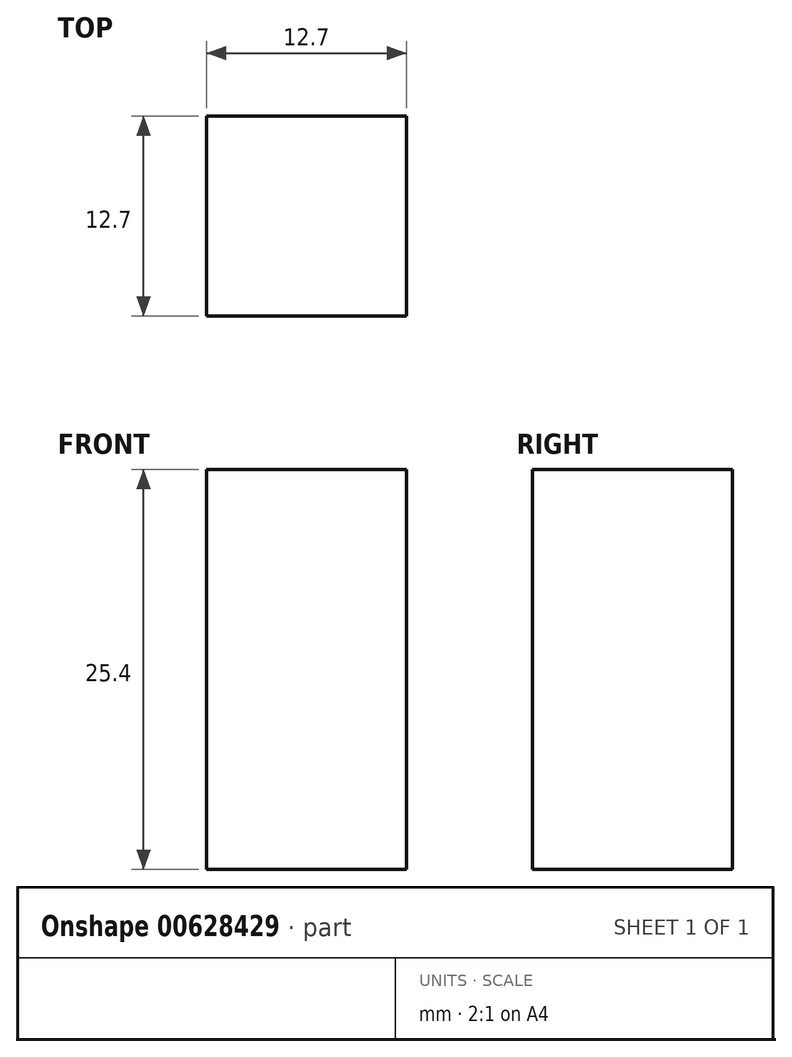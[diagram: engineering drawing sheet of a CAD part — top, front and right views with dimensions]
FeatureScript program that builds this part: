
annotation { "Feature Type Name" : "Feature", "Feature Type Description" : "" }
export const myFeature = defineFeature(function(context is Context, id is Id, definition is map)
    precondition{}
    {
        {
            var Q0;
            Q0=qCreatedBy(makeId("Top.planeOp"),FACE);
            var sketch = newSketch(context, id + "F0", { "sketchPlane" : qUnion([Q0])});
            skLineSegment(sketch, "E0.bottom", {"start": v(0, 0) * mm, "end": v(12.7, 0) * mm});
            skLineSegment(sketch, "E0.top", {"start": v(0, 12.7) * mm, "end": v(12.7, 12.7) * mm});
            skLineSegment(sketch, "E0.left", {"start": v(0, 0) * mm, "end": v(0, 12.7) * mm});
            skLineSegment(sketch, "E0.right", {"start": v(12.7, 0) * mm, "end": v(12.7, 12.7) * mm});
            skSolve(sketch);
        }
        {
            var Q0;
            Q0=makeQuery(id+"F0.imprint","IMPRINT",FACE,{"disambiguationData":[TD([[makeQuery(id+"F0.imprint","IMPRINT",EDGE,{"derivedFrom":sQuery(id+"F0.wireOp",EDGE,"E0.bottom")}),1.0]])]});
            extrude(context, id + "F1", {"entities" : qUnion([Q0]), "depth" : 25.4 * mm, "offsetDistance" : 25.4 * mm});
        }
    });
